# Revit family: Pre-rinse mach curv R-L Metos WD PRM90_4196677
name_source: partatom
category: Specialty Equipment
revit_build: Autodesk Revit 2018 (Build: 20180423_1000(x64)
units: mm (PartAtom-declared; Revit-internal decimal feet)

## family parameters
Always vertical = Yes
Cut with Voids When Loaded = No
OmniClass Number = 23.45.30.14.11
OmniClass Title = Commercial Dishwashers
Part Type = Normal
Room Calculation Point = No
Round Connector Dimension = Use Diameter
Shared = No
Work Plane-Based = No

## types (1)
- Pre-rinse mach curv R-L Metos WD PRM90_4196677
    Cold Water Connection Height = 0 mm  [stored 0 ft]
    Cold Water Flow = 0.0 L/min
    Cold Water Maximum Pressure = 0.0 Pa
    Cold Water Minimum Pressure = 0.0 Pa
    Conn Plug = Semifixed
    Cycle = 50 Hz
    Depth Actual = 950 mm  [stored 3.1168 ft]
    Description = Pre-rinse mach. curv. R-L Metos WD PRM90
    Direct Waste Connection Height = 0 mm  [stored 0 ft]
    Direct Waste Flow = 180.0 L/min
    Direct Waste Size = 50
    Elec Conn Connection Height = 0 mm  [stored 0 ft]
    FL Amps = 10 A
    Foodservice Equipment Identifier = Yes
    Height Actual = 1700 mm  [stored 5.57743 ft]
    Hot Water Connection Height = 0 mm  [stored 0 ft]
    Hot Water Flow = 0.0 L/min
    Hot Water Maximum Pressure = 0.0 Pa
    Hot Water Minimum Pressure = 0.0 Pa
    Item Number = 4196677
    Latent Heat Output = 0 W
    Length Actual = 950 mm  [stored 3.1168 ft]
    Metos Phase  = 3NPE
    Operational Current = 0 A
    Price = 0 $
    Refrigerant Mass = 0.00 kg
    Sensitive Heat Output = 0 W
    URL Manufacturer = https://www.metos.com
    Volts = 400 V
    Watts = 750 W
    Weight = 250

note: [stored X ft] marks values corroborated as IEEE doubles in the binary element streams (Revit-internal decimal feet)

## geometry (parser evidence)
native form markers: Sweep x2
no freeform markers — native parametric forms only
